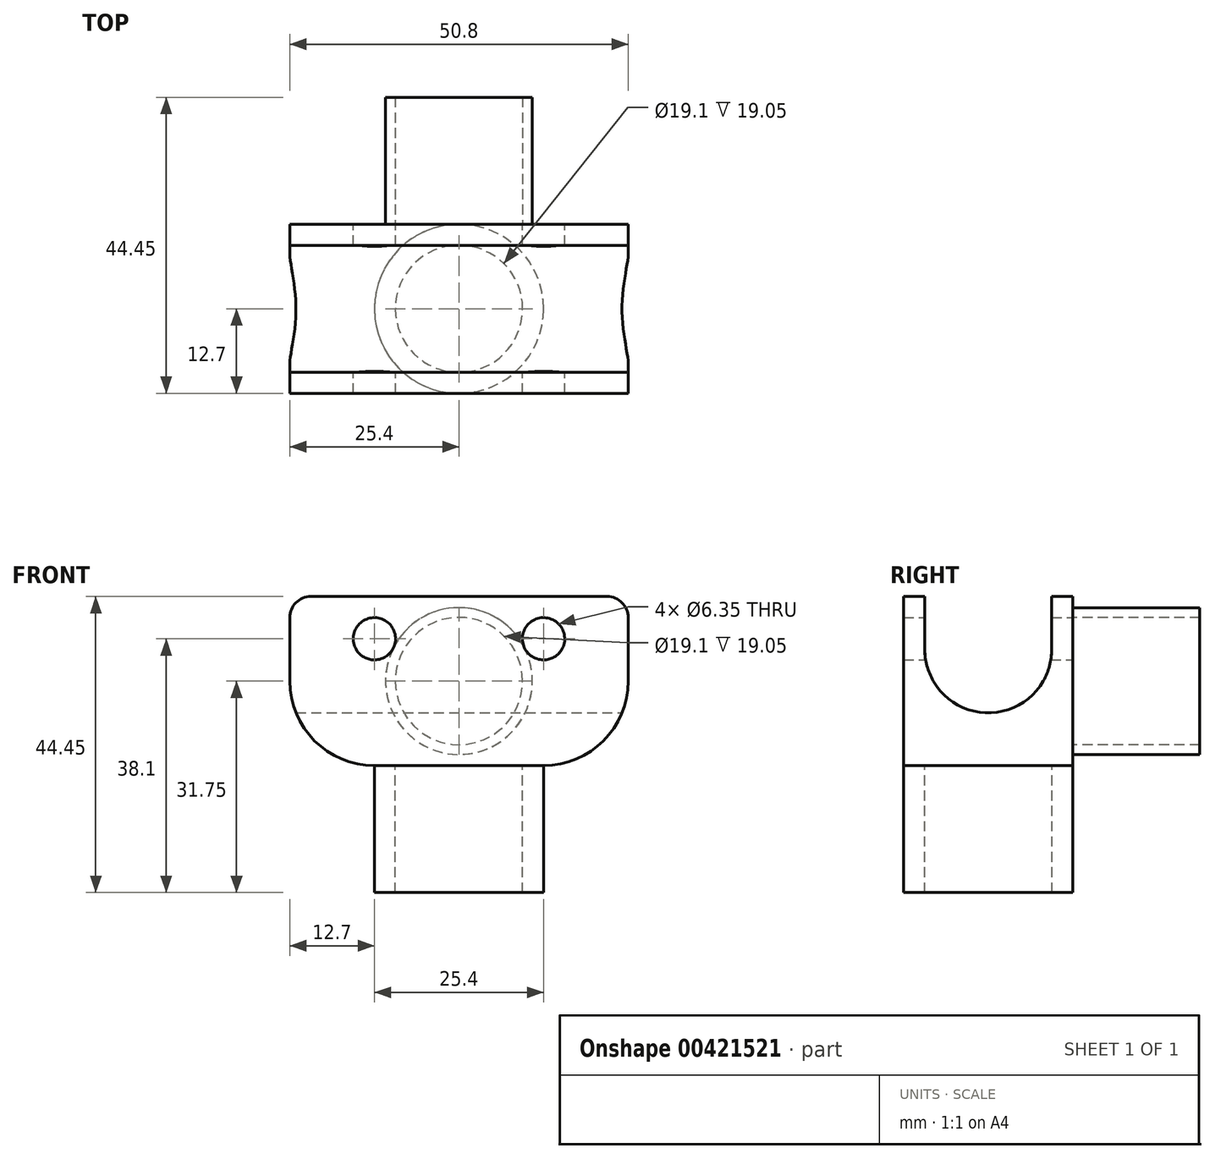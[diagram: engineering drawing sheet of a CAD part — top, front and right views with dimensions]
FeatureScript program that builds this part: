
annotation { "Feature Type Name" : "Feature", "Feature Type Description" : "" }
export const myFeature = defineFeature(function(context is Context, id is Id, definition is map)
    precondition{}
    {
        {
            var Q0;
            Q0=qCreatedBy(makeId("Front.planeOp"),FACE);
            var sketch = newSketch(context, id + "F0", { "sketchPlane" : qUnion([Q0])});
            skLineSegment(sketch, "E0", {"start": v(0, 0) * mm, "end": v(12.7, 0) * mm});
            skLineSegment(sketch, "E1", {"start": v(25.4, 12.7) * mm, "end": v(25.4, 22.23) * mm});
            skLineSegment(sketch, "E2", {"start": v(22.23, 25.4) * mm, "end": v(0, 25.4) * mm});
            skLineSegment(sketch, "E3", {"start": v(0, 25.4) * mm, "end": v(-22.22, 25.4) * mm});
            skLineSegment(sketch, "E4", {"start": v(-25.4, 22.22) * mm, "end": v(-25.4, 12.7) * mm});
            skLineSegment(sketch, "E5", {"start": v(-12.7, 0) * mm, "end": v(0, 0) * mm});
            skPoint(sketch, "E6.visualSharp", {"position": v(-25.4, 0) * mm});
            skArc(sketch, "E6.filletArc", {"start": v(-25.4, 12.7) * mm, "mid": v(-21.68, 3.72) * mm, "end": v(-12.7, 0) * mm});
            skPoint(sketch, "E7.visualSharp", {"position": v(25.4, 0) * mm});
            skArc(sketch, "E7.filletArc", {"start": v(12.7, 0) * mm, "mid": v(21.68, 3.72) * mm, "end": v(25.4, 12.7) * mm});
            skCircle(sketch, "E8", {"center": v(12.7, 19.05) * mm, "radius": 3.18 * mm});
            skPoint(sketch, "E9.orphan", {"position": v(0, 19.05) * mm});
            skPoint(sketch, "E10.orphan", {"position": v(25.4, 19.05) * mm});
            skCircle(sketch, "E11", {"center": v(-12.7, 19.05) * mm, "radius": 3.18 * mm});
            skPoint(sketch, "E11.centerSnap0", {"position": v(-25.4, 19.05) * mm});
            skPoint(sketch, "E11.centerSnap1", {"position": v(-12.7, 25.4) * mm});
            skPoint(sketch, "E12.visualSharp", {"position": v(-25.4, 25.4) * mm});
            skArc(sketch, "E12.filletArc", {"start": v(-22.22, 25.4) * mm, "mid": v(-24.47, 24.47) * mm, "end": v(-25.4, 22.22) * mm});
            skPoint(sketch, "E13.visualSharp", {"position": v(25.4, 25.4) * mm});
            skArc(sketch, "E13.filletArc", {"start": v(25.4, 22.23) * mm, "mid": v(24.47, 24.47) * mm, "end": v(22.23, 25.4) * mm});
            skSolve(sketch);
        }
        {
            var Q0;
            Q0 = qSketchRegion(id + "F0", true);
            extrude(context, id + "F1", {"entities" : qUnion([Q0]), "depth" : 25.4 * mm});
        }
        {
            var Q0;
            Q0=makeQuery(id+"F1.opExtrude","SWEPT_FACE",FACE,{"disambiguationData":[OSD([sQuery(id+"F0.wireOp",EDGE,"E1")])]});
            var sketch = newSketch(context, id + "F2", { "sketchPlane" : qUnion([Q0])});
            skArc(sketch, "E14", {"start": v(-22.23, 17.46) * mm, "mid": v(-12.7, 7.94) * mm, "end": v(-3.18, 17.46) * mm});
            skPoint(sketch, "E15.orphan", {"position": v(-25.4, 17.46) * mm});
            skPoint(sketch, "E16.end.orphan", {"position": v(0, 17.46) * mm});
            skLineSegment(sketch, "E17", {"start": v(-22.23, 17.46) * mm, "end": v(-22.23, 31.53) * mm});
            skLineSegment(sketch, "E18", {"start": v(-22.23, 31.53) * mm, "end": v(-3.18, 31.53) * mm});
            skLineSegment(sketch, "E19", {"start": v(-3.18, 17.46) * mm, "end": v(-3.18, 31.53) * mm});
            skSolve(sketch);
        }
        {
            var Q0;
            Q0 = qSketchRegion(id + "F2", true);
            extrude(context, id + "F3", {"entities" : qUnion([Q0]), "operationType" : NewBodyOperationType.REMOVE, "endBound" : BoundingType.THROUGH_ALL, "oppositeDirection" : true, "depth" : 25.4 * mm});
        }
        {
            var Q0;
            Q0=makeQuery(id+"F1.opExtrude","SWEPT_FACE",FACE,{"disambiguationData":[OSD([sQuery(id+"F0.wireOp",EDGE,"E0"),sQuery(id+"F0.wireOp",EDGE,"E5")])]});
            var sketch = newSketch(context, id + "F4", { "sketchPlane" : qUnion([Q0])});
            skCircle(sketch, "E20", {"center": v(0, 12.7) * mm, "radius": 9.55 * mm});
            skCircle(sketch, "E21", {"center": v(0, 12.7) * mm, "radius": 12.7 * mm});
            skSolve(sketch);
        }
        {
            var Q0;
            Q0 = qSketchRegion(id + "F4", true);
            extrude(context, id + "F5", {"entities" : qUnion([Q0]), "operationType" : NewBodyOperationType.ADD, "depth" : 19.05 * mm});
        }
        {
            var Q0;
            Q0=makeQuery(id+"F1.opExtrude","CAP_FACE",FACE,{"disambiguationData":[OSD([sQuery(id+"F0.wireOp",EDGE,"E0"),sQuery(id+"F0.wireOp",EDGE,"E1"),sQuery(id+"F0.wireOp",EDGE,"E2"),sQuery(id+"F0.wireOp",EDGE,"E3"),sQuery(id+"F0.wireOp",EDGE,"E4"),sQuery(id+"F0.wireOp",EDGE,"E5"),sQuery(id+"F0.wireOp",EDGE,"E6.filletArc"),sQuery(id+"F0.wireOp",EDGE,"E7.filletArc"),sQuery(id+"F0.wireOp",EDGE,"E8"),sQuery(id+"F0.wireOp",EDGE,"E11"),sQuery(id+"F0.wireOp",EDGE,"E12.filletArc"),sQuery(id+"F0.wireOp",EDGE,"E13.filletArc")])],"isStart":true});
            var sketch = newSketch(context, id + "F6", { "sketchPlane" : qUnion([Q0])});
            skCircle(sketch, "E22", {"center": v(0, 12.7) * mm, "radius": 11.02 * mm});
            skCircle(sketch, "E23", {"center": v(0, 12.7) * mm, "radius": 9.55 * mm});
            skSolve(sketch);
        }
        {
            var Q0;
            Q0 = qSketchRegion(id + "F6", true);
            extrude(context, id + "F7", {"entities" : qUnion([Q0]), "operationType" : NewBodyOperationType.ADD, "depth" : 19.05 * mm});
        }
    });
